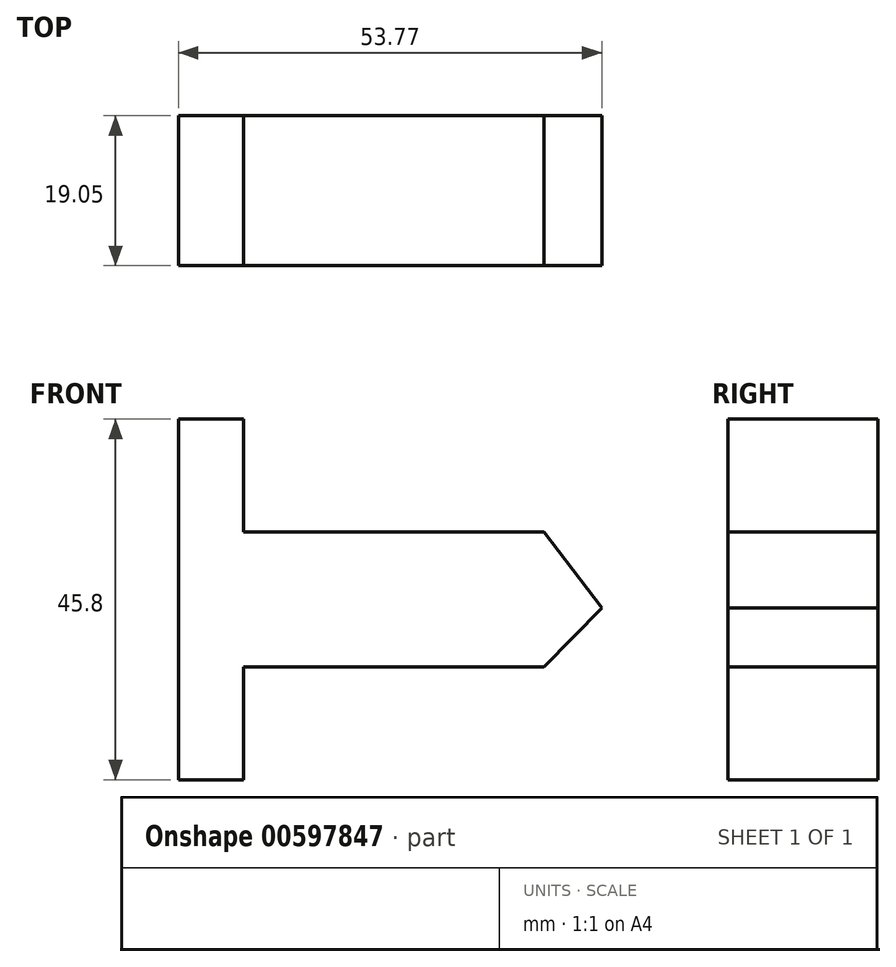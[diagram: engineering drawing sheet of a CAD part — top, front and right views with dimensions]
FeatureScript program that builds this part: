
annotation { "Feature Type Name" : "Feature", "Feature Type Description" : "" }
export const myFeature = defineFeature(function(context is Context, id is Id, definition is map)
    precondition{}
    {
        {
            var Q0;
            Q0=qCreatedBy(makeId("Front.planeOp"),FACE);
            var sketch = newSketch(context, id + "F0", { "sketchPlane" : qUnion([Q0])});
            skLineSegment(sketch, "E0", {"start": v(0, 23.97) * mm, "end": v(0, -21.83) * mm});
            skLineSegment(sketch, "E1", {"start": v(3.82, -21.83) * mm, "end": v(3.82, 23.97) * mm});
            skLineSegment(sketch, "E2", {"start": v(3.82, 23.97) * mm, "end": v(0, 23.97) * mm});
            skLineSegment(sketch, "E3", {"start": v(0, -21.83) * mm, "end": v(3.82, -21.83) * mm});
            skLineSegment(sketch, "E4", {"start": v(3.82, 0) * mm, "end": v(49.32, 0) * mm});
            skLineSegment(sketch, "E5", {"start": v(49.32, 0) * mm, "end": v(41.99, 9.62) * mm});
            skLineSegment(sketch, "E6", {"start": v(41.99, 9.62) * mm, "end": v(3.82, 9.62) * mm});
            skLineSegment(sketch, "E7", {"start": v(41.99, -7.48) * mm, "end": v(49.32, 0) * mm});
            skLineSegment(sketch, "E8", {"start": v(41.99, -7.48) * mm, "end": v(3.82, -7.48) * mm});
            skFitSpline(sketch, "E9", {"points": [v(0, 0) * mm, v(-11.15, 5.95) * mm, v(-27.33, 6.26) * mm, v(-11.76, 3.2) * mm, v(-8.4, 0) * mm, v(-25.2, -3.82) * mm, v(-9.92, -3.82) * mm, v(0, 0) * mm]});
            skSolve(sketch);
        }
        {
            var Q0;
            {var subQ8=sQuery(id+"F0.wireOp",EDGE,"E2");Q0=makeQuery(id+"F0.imprint","IMPRINT",FACE,{"disambiguationData":[TD([[makeQuery(id+"F0.imprint","IMPRINT",EDGE,{"derivedFrom":subQ8}),1.0]])]});}
            var Q1;
            {var subQ0=sQuery(id+"F0.wireOp",EDGE,"E9");var subQ1=sQuery(id+"F0.wireOp",EDGE,"E0");var subQ2=makeQuery(id+"F0.imprint","INTERSECT",VERTEX,{"disambiguationData":[OD(0.0)],"derivedFrom":[subQ1,subQ0]});Q1=makeQuery(id+"F0.imprint","IMPRINT",FACE,{"disambiguationData":[TD([[makeQuery(id+"F0.imprint","IMPRINT",EDGE,{"disambiguationData":[TD([[subQ2,1.0]])],"derivedFrom":subQ0}),1.0]])]});}
            var Q2;
            {var subQ0=sQuery(id+"F0.wireOp",EDGE,"E4");Q2=makeQuery(id+"F0.imprint","IMPRINT",FACE,{"disambiguationData":[TD([[makeQuery(id+"F0.imprint","IMPRINT",EDGE,{"derivedFrom":subQ0}),1.0]])]});}
            var Q3;
            {var subQ0=sQuery(id+"F0.wireOp",EDGE,"E4");Q3=makeQuery(id+"F0.imprint","IMPRINT",FACE,{"disambiguationData":[TD([[makeQuery(id+"F0.imprint","IMPRINT",EDGE,{"derivedFrom":subQ0}),-1.0]])]});}
            extrude(context, id + "F1", {"entities" : qUnion([Q0, Q1, Q2, Q3]), "depth" : 12.7 * mm, "offsetDistance" : 25.4 * mm});
        }
        {
            var Q0;
            {var subQ0=sQuery(id+"F0.wireOp",EDGE,"E0");Q0=makeQuery(id+"F1.opExtrude","SWEPT_FACE",FACE,{"disambiguationData":[OSD([subQ0]),TDD([makeQuery(id+"F0.imprint","IMPRINT",EDGE,{"disambiguationData":[TD([[makeQuery(id+"F0.imprint","INTERSECT",VERTEX,{"derivedFrom":[subQ0,sQuery(id+"F0.wireOp",EDGE,"E2")]}),-1.0]])],"derivedFrom":subQ0})])]});}
            var Q1;
            {var subQ0=sQuery(id+"F0.wireOp",EDGE,"E0");Q1=makeQuery(id+"F1.opExtrude","SWEPT_FACE",FACE,{"disambiguationData":[OSD([subQ0]),TDD([makeQuery(id+"F0.imprint","IMPRINT",EDGE,{"disambiguationData":[TD([[makeQuery(id+"F0.imprint","INTERSECT",VERTEX,{"derivedFrom":[subQ0,sQuery(id+"F0.wireOp",EDGE,"E3")]}),1.0]])],"derivedFrom":subQ0})])]});}
            extrude(context, id + "F2", {"entities" : qUnion([Q0, Q1]), "operationType" : NewBodyOperationType.ADD, "depth" : 0.64 * mm, "offsetDistance" : 25.4 * mm});
        }
        {
            var Q0;
            {var subQ0=sQuery(id+"F0.wireOp",EDGE,"E0");Q0=makeQuery(id+"F2.opExtrude","CAP_FACE",FACE,{"disambiguationData":[OSD([subQ0]),TDD([makeQuery(id+"F1.opExtrude","SWEPT_FACE",FACE,{"disambiguationData":[OSD([subQ0]),TDD([makeQuery(id+"F0.imprint","IMPRINT",EDGE,{"disambiguationData":[TD([[makeQuery(id+"F0.imprint","INTERSECT",VERTEX,{"derivedFrom":[subQ0,sQuery(id+"F0.wireOp",EDGE,"E2")]}),-1.0]])],"derivedFrom":subQ0})])]})])],"isStart":false});}
            var Q1;
            {var subQ0=sQuery(id+"F0.wireOp",EDGE,"E0");Q1=makeQuery(id+"F2.opExtrude","CAP_FACE",FACE,{"disambiguationData":[OSD([subQ0]),TDD([makeQuery(id+"F1.opExtrude","SWEPT_FACE",FACE,{"disambiguationData":[OSD([subQ0]),TDD([makeQuery(id+"F0.imprint","IMPRINT",EDGE,{"disambiguationData":[TD([[makeQuery(id+"F0.imprint","INTERSECT",VERTEX,{"derivedFrom":[subQ0,sQuery(id+"F0.wireOp",EDGE,"E3")]}),1.0]])],"derivedFrom":subQ0})])]})])],"isStart":false});}
            extrude(context, id + "F3", {"entities" : qUnion([Q0, Q1]), "operationType" : NewBodyOperationType.ADD, "depth" : 3.8 * mm, "offsetDistance" : 25.4 * mm});
        }
        {
            var Q0;
            {var subQ0=sQuery(id+"F0.wireOp",EDGE,"E3");var subQ1=sQuery(id+"F0.wireOp",EDGE,"E0");var subQ2=sQuery(id+"F0.wireOp",EDGE,"E9");var subQ3=makeQuery(id+"F1.opExtrude","CAP_EDGE",EDGE,{"disambiguationData":[OSD([subQ1]),TDD([makeQuery(id+"F0.imprint","IMPRINT",EDGE,{"disambiguationData":[TD([[makeQuery(id+"F0.imprint","INTERSECT",VERTEX,{"derivedFrom":[subQ1,subQ0]}),1.0]])],"derivedFrom":subQ1})])],"isStart":false});var subQ4=sQuery(id+"F0.wireOp",EDGE,"E2");var subQ5=makeQuery(id+"F1.opExtrude","CAP_EDGE",EDGE,{"disambiguationData":[OSD([subQ1]),TDD([makeQuery(id+"F0.imprint","IMPRINT",EDGE,{"disambiguationData":[TD([[makeQuery(id+"F0.imprint","INTERSECT",VERTEX,{"derivedFrom":[subQ1,subQ4]}),-1.0]])],"derivedFrom":subQ1})])],"isStart":false});Q0=makeQuery(id+"F3.boolean.opBoolean","MERGE",FACE,{"derivedFrom":[makeQuery(id+"F2.boolean.opBoolean","MERGE",FACE,{"derivedFrom":[makeQuery(id+"F1.opExtrude","CAP_FACE",FACE,{"disambiguationData":[OSD([subQ1,sQuery(id+"F0.wireOp",EDGE,"E1"),subQ4,subQ0,sQuery(id+"F0.wireOp",EDGE,"E5"),sQuery(id+"F0.wireOp",EDGE,"E6"),sQuery(id+"F0.wireOp",EDGE,"E7"),sQuery(id+"F0.wireOp",EDGE,"E8"),subQ2])],"isStart":false}),makeQuery(id+"F2.opExtrude","SWEPT_FACE",FACE,{"disambiguationData":[OSD([subQ1]),TDD([subQ5])]}),makeQuery(id+"F2.opExtrude","SWEPT_FACE",FACE,{"disambiguationData":[OSD([subQ1]),TDD([subQ3])]})]}),makeQuery(id+"F3.opExtrude","SWEPT_FACE",FACE,{"disambiguationData":[OSD([subQ1]),TDD([makeQuery(id+"F2.opExtrude","CAP_EDGE",EDGE,{"disambiguationData":[OSD([subQ1]),TDD([subQ5])],"isStart":false})])]}),makeQuery(id+"F3.opExtrude","SWEPT_FACE",FACE,{"disambiguationData":[OSD([subQ1]),TDD([makeQuery(id+"F2.opExtrude","CAP_EDGE",EDGE,{"disambiguationData":[OSD([subQ1]),TDD([subQ3])],"isStart":false})])]})]});}
            extrude(context, id + "F4", {"entities" : qUnion([Q0]), "operationType" : NewBodyOperationType.ADD, "depth" : 6.35 * mm, "offsetDistance" : 25.4 * mm});
        }
    });
